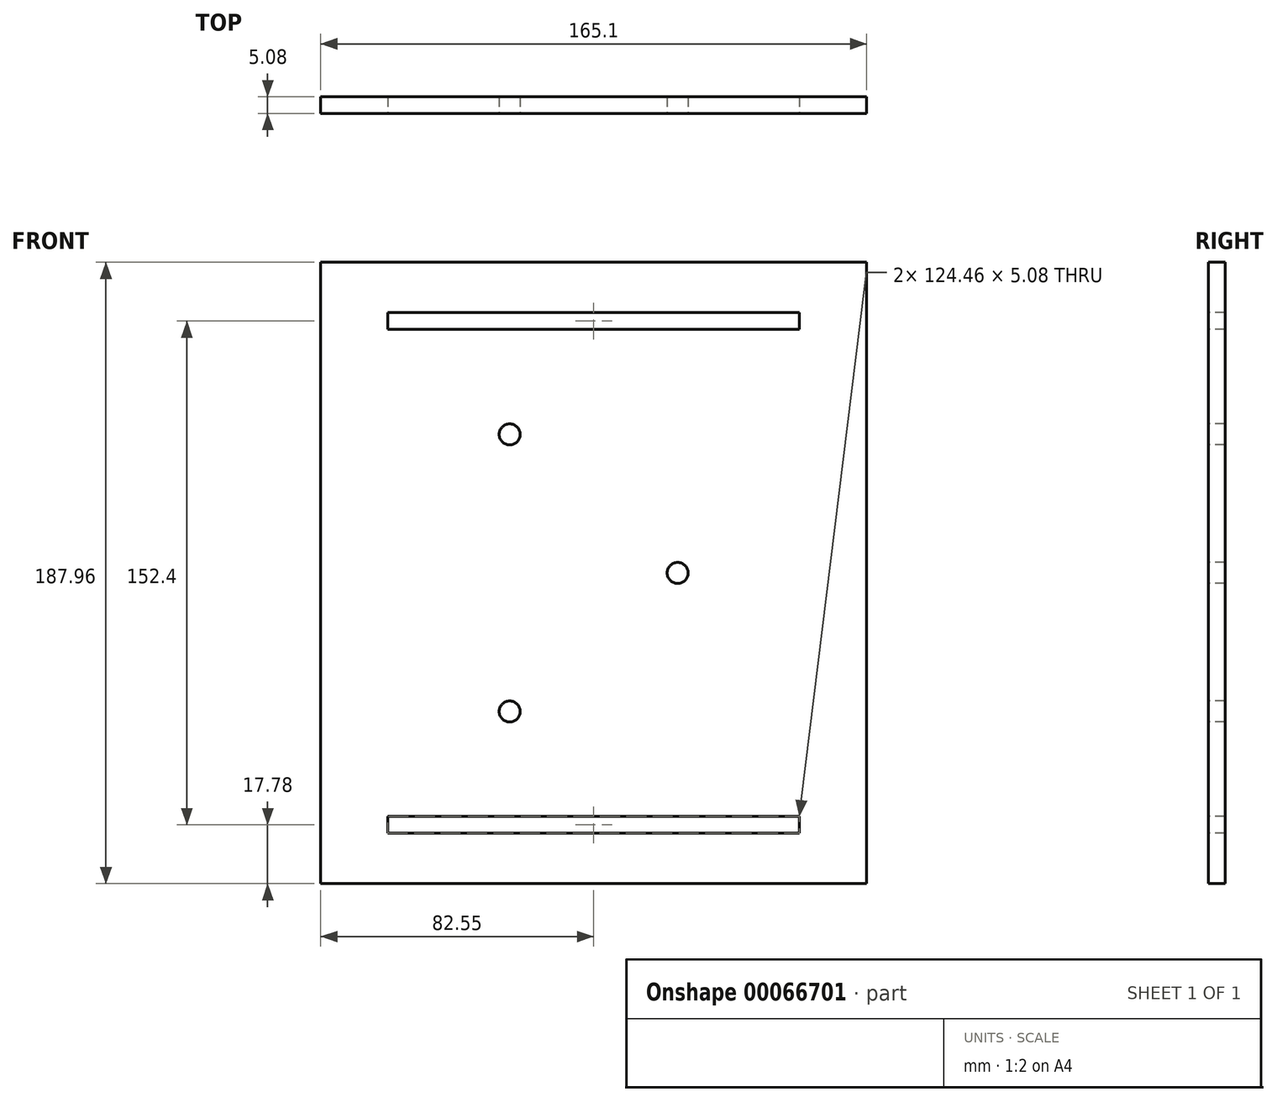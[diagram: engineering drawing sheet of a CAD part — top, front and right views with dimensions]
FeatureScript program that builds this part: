
annotation { "Feature Type Name" : "Feature", "Feature Type Description" : "" }
export const myFeature = defineFeature(function(context is Context, id is Id, definition is map)
    precondition{}
    {
        {
            var Q0;
            Q0=qCreatedBy(makeId("Front.planeOp"),FACE);
            var sketch = newSketch(context, id + "F0", { "sketchPlane" : qUnion([Q0])});
            skLineSegment(sketch, "E0.bottom", {"start": v(0, 0) * mm, "end": v(165.1, 0) * mm});
            skLineSegment(sketch, "E0.top", {"start": v(0, -187.96) * mm, "end": v(165.1, -187.96) * mm});
            skLineSegment(sketch, "E0.left", {"start": v(0, 0) * mm, "end": v(0, -187.96) * mm});
            skLineSegment(sketch, "E0.right", {"start": v(165.1, 0) * mm, "end": v(165.1, -187.96) * mm});
            skSolve(sketch);
        }
        {
            var Q0;
            Q0 = qSketchRegion(id + "F0", true);
            extrude(context, id + "F1", {"entities" : qUnion([Q0]), "depth" : 5.08 * mm});
        }
        {
            var Q0;
            Q0=makeQuery(id+"F1.opExtrude","CAP_FACE",FACE,{"disambiguationData":[OSD([sQuery(id+"F0.wireOp",EDGE,"E0.bottom"),sQuery(id+"F0.wireOp",EDGE,"E0.top"),sQuery(id+"F0.wireOp",EDGE,"E0.left"),sQuery(id+"F0.wireOp",EDGE,"E0.right")])],"isStart":false});
            var sketch = newSketch(context, id + "F2", { "sketchPlane" : qUnion([Q0])});
            skLineSegment(sketch, "E1.bottom", {"start": v(0, 0) * mm, "end": v(20.32, 0) * mm});
            skLineSegment(sketch, "E1.top", {"start": v(0, -20.32) * mm, "end": v(20.32, -20.32) * mm});
            skLineSegment(sketch, "E1.left", {"start": v(0, 0) * mm, "end": v(0, -20.32) * mm});
            skLineSegment(sketch, "E1.right", {"start": v(20.32, 0) * mm, "end": v(20.32, -20.32) * mm});
            skLineSegment(sketch, "E2.bottom", {"start": v(20.32, -20.32) * mm, "end": v(144.78, -20.32) * mm});
            skLineSegment(sketch, "E3.bottom", {"start": v(165.1, 0) * mm, "end": v(144.78, 0) * mm});
            skLineSegment(sketch, "E3.top", {"start": v(165.1, -20.32) * mm, "end": v(144.78, -20.32) * mm});
            skLineSegment(sketch, "E3.left", {"start": v(165.1, 0) * mm, "end": v(165.1, -20.32) * mm});
            skLineSegment(sketch, "E3.right", {"start": v(144.78, 0) * mm, "end": v(144.78, -20.32) * mm});
            skLineSegment(sketch, "E4", {"start": v(20.32, -15.24) * mm, "end": v(144.78, -15.24) * mm});
            skLineSegment(sketch, "E5", {"start": v(-17.21, -93.98) * mm, "end": v(252.26, -93.98) * mm, "construction": true});
            skLineSegment(sketch, "E6.MirrorCS", {"start": v(20.32, -167.64) * mm, "end": v(144.78, -167.64) * mm});
            skLineSegment(sketch, "E7.MirrorCS", {"start": v(20.32, -172.72) * mm, "end": v(144.78, -172.72) * mm});
            skLineSegment(sketch, "E8.MirrorCS", {"start": v(144.78, -187.96) * mm, "end": v(144.78, -167.64) * mm});
            skLineSegment(sketch, "E9.MirrorCS", {"start": v(165.1, -167.64) * mm, "end": v(144.78, -167.64) * mm});
            skLineSegment(sketch, "E10.MirrorCS", {"start": v(165.1, -187.96) * mm, "end": v(165.1, -167.64) * mm});
            skLineSegment(sketch, "E11.MirrorCS", {"start": v(20.32, -187.96) * mm, "end": v(20.32, -167.64) * mm});
            skLineSegment(sketch, "E12.MirrorCS", {"start": v(0, -167.64) * mm, "end": v(20.32, -167.64) * mm});
            skSolve(sketch);
        }
        {
            var Q0;
            {var subQ0=sQuery(id+"F2.wireOp",EDGE,"E2.bottom");Q0=makeQuery(id+"F2.imprint","IMPRINT",FACE,{"disambiguationData":[TD([[makeQuery(id+"F2.imprint","IMPRINT",EDGE,{"derivedFrom":subQ0}),1.0]])]});}
            var Q1;
            {var subQ0=sQuery(id+"F2.wireOp",EDGE,"E6.MirrorCS");Q1=makeQuery(id+"F2.imprint","IMPRINT",FACE,{"disambiguationData":[TD([[makeQuery(id+"F2.imprint","IMPRINT",EDGE,{"derivedFrom":subQ0}),-1.0]])]});}
            extrude(context, id + "F3", {"entities" : qUnion([Q0, Q1]), "operationType" : NewBodyOperationType.REMOVE, "oppositeDirection" : true, "depth" : 25.4 * mm});
        }
        {
            var Q0;
            Q0=makeQuery(id+"F1.opExtrude","CAP_FACE",FACE,{"disambiguationData":[OSD([sQuery(id+"F0.wireOp",EDGE,"E0.bottom"),sQuery(id+"F0.wireOp",EDGE,"E0.top"),sQuery(id+"F0.wireOp",EDGE,"E0.left"),sQuery(id+"F0.wireOp",EDGE,"E0.right")])],"isStart":false});
            var sketch = newSketch(context, id + "F4", { "sketchPlane" : qUnion([Q0])});
            skLineSegment(sketch, "E13", {"start": v(0, -93.98) * mm, "end": v(57.15, -93.98) * mm});
            skPoint(sketch, "E13.endSnap0", {"position": v(0, -93.98) * mm});
            skLineSegment(sketch, "E14", {"start": v(57.15, -52.07) * mm, "end": v(57.15, -135.9) * mm});
            skCircle(sketch, "E15", {"center": v(57.15, -52.07) * mm, "radius": 3.18 * mm});
            skCircle(sketch, "E16", {"center": v(57.15, -135.9) * mm, "radius": 3.18 * mm});
            skLineSegment(sketch, "E17", {"start": v(57.15, -93.98) * mm, "end": v(107.95, -93.98) * mm});
            skCircle(sketch, "E18", {"center": v(107.95, -93.98) * mm, "radius": 3.18 * mm});
            skSolve(sketch);
        }
        {
            var Q0;
            Q0 = qSketchRegion(id + "F4", true);
            extrude(context, id + "F5", {"entities" : qUnion([Q0]), "operationType" : NewBodyOperationType.REMOVE, "oppositeDirection" : true, "depth" : 25.4 * mm});
        }
    });
